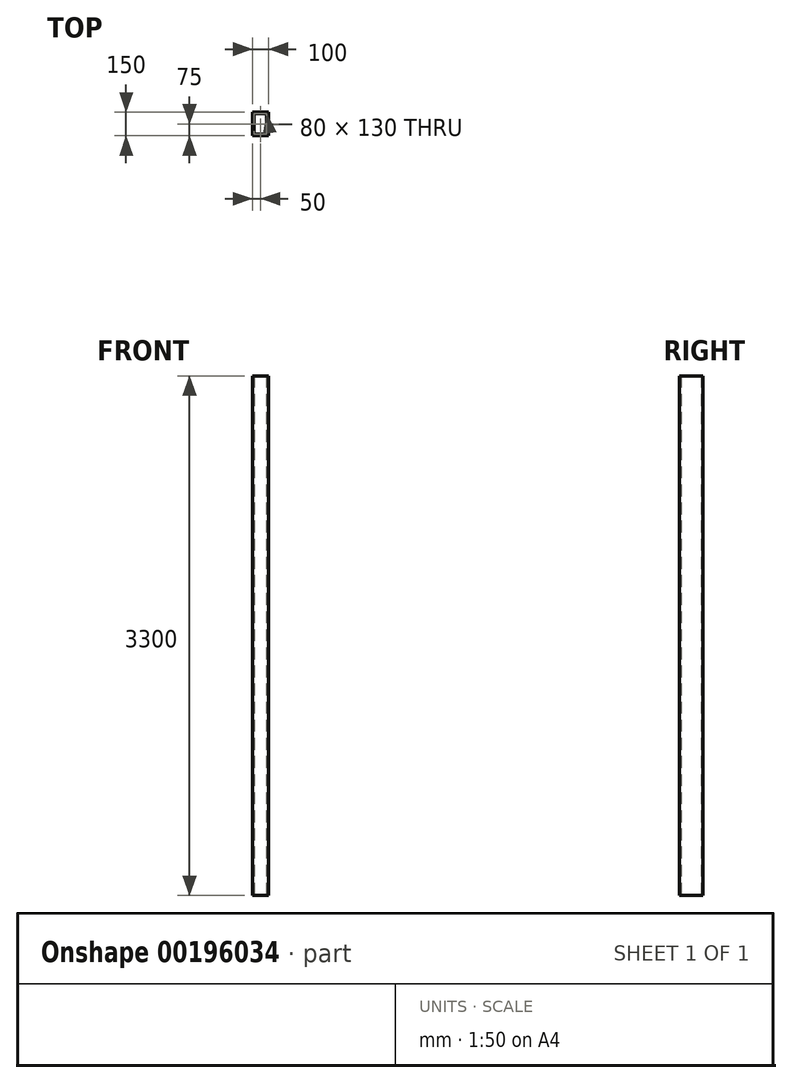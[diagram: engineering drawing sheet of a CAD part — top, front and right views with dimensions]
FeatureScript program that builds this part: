
annotation { "Feature Type Name" : "Feature", "Feature Type Description" : "" }
export const myFeature = defineFeature(function(context is Context, id is Id, definition is map)
    precondition{}
    {
        {
            var Q0;
            Q0=qCreatedBy(makeId("Top.planeOp"),FACE);
            var sketch = newSketch(context, id + "F0", { "sketchPlane" : qUnion([Q0])});
            skLineSegment(sketch, "E0", {"start": v(0, 173.7) * mm, "end": v(0, -178.57) * mm, "construction": true});
            skLineSegment(sketch, "E1", {"start": v(-156.9, 0) * mm, "end": v(160.53, 0) * mm, "construction": true});
            skLineSegment(sketch, "E2.bottom", {"start": v(-50, 75) * mm, "end": v(50, 75) * mm});
            skLineSegment(sketch, "E2.top", {"start": v(-50, -75) * mm, "end": v(50, -75) * mm});
            skLineSegment(sketch, "E2.left", {"start": v(-50, 75) * mm, "end": v(-50, -75) * mm});
            skLineSegment(sketch, "E2.right", {"start": v(50, 75) * mm, "end": v(50, -75) * mm});
            skLineSegment(sketch, "E3.bottom", {"start": v(-40, 65) * mm, "end": v(40, 65) * mm});
            skLineSegment(sketch, "E3.top", {"start": v(-40, -65) * mm, "end": v(40, -65) * mm});
            skLineSegment(sketch, "E3.left", {"start": v(-40, 65) * mm, "end": v(-40, -65) * mm});
            skLineSegment(sketch, "E3.right", {"start": v(40, 65) * mm, "end": v(40, -65) * mm});
            skSolve(sketch);
        }
        {
            var Q0;
            Q0 = qSketchRegion(id + "F0", true);
            extrude(context, id + "F1", {"entities" : qUnion([Q0]), "depth" : 3300 * mm});
        }
    });
